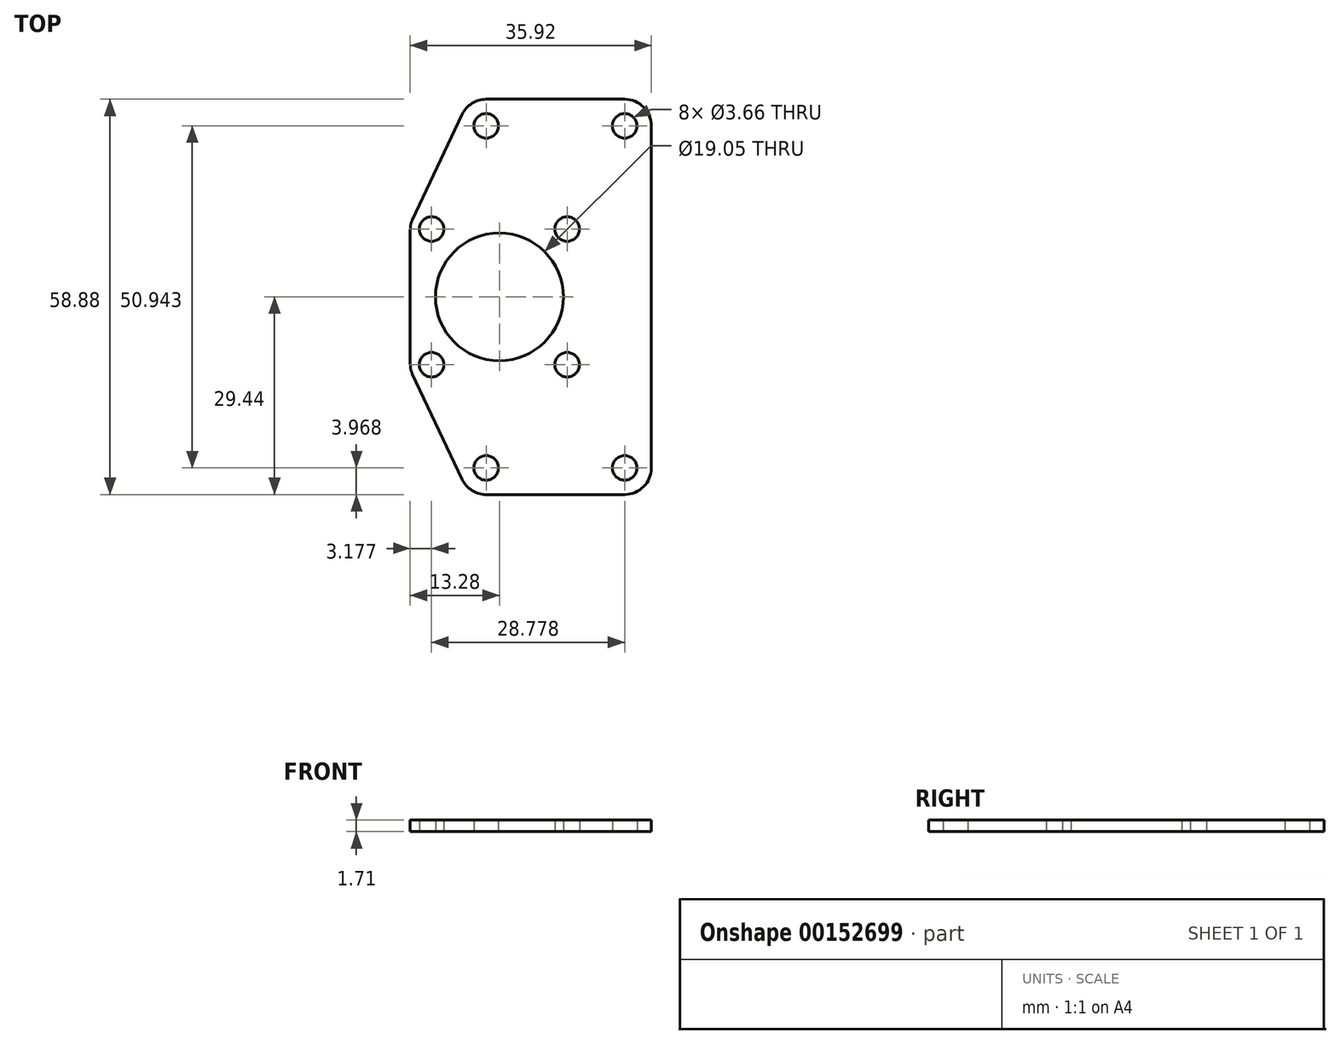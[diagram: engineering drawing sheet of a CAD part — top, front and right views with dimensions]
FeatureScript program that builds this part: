
annotation { "Feature Type Name" : "Feature", "Feature Type Description" : "" }
export const myFeature = defineFeature(function(context is Context, id is Id, definition is map)
    precondition{}
    {
        {
            var Q0;
            Q0=qCreatedBy(makeId("Top.planeOp"),FACE);
            var sketch = newSketch(context, id + "F0", { "sketchPlane" : qUnion([Q0])});
            skLineSegment(sketch, "E0.bottom", {"start": v(10.1, 10.1) * mm, "end": v(-10.1, 10.1) * mm, "construction": true});
            skLineSegment(sketch, "E0.top", {"start": v(10.1, -10.1) * mm, "end": v(-10.1, -10.1) * mm, "construction": true});
            skLineSegment(sketch, "E0.left", {"start": v(10.1, 10.1) * mm, "end": v(10.1, -10.1) * mm, "construction": true});
            skLineSegment(sketch, "E0.right", {"start": v(-10.1, 10.1) * mm, "end": v(-10.1, -10.1) * mm, "construction": true});
            skPoint(sketch, "E0.middle", {"position": v(0, 0) * mm});
            skCircle(sketch, "E1", {"center": v(0, 0) * mm, "radius": 9.53 * mm});
            skCircle(sketch, "E2", {"center": v(-10.1, 10.1) * mm, "radius": 1.83 * mm});
            skCircle(sketch, "E3", {"center": v(10.1, 10.1) * mm, "radius": 1.83 * mm});
            skCircle(sketch, "E4", {"center": v(10.1, -10.1) * mm, "radius": 1.83 * mm});
            skCircle(sketch, "E5", {"center": v(-10.1, -10.1) * mm, "radius": 1.83 * mm});
            skLineSegment(sketch, "E6", {"start": v(0, 0) * mm, "end": v(-13.28, 0) * mm, "construction": true});
            skLineSegment(sketch, "E7", {"start": v(0, 0) * mm, "end": v(22.64, 0) * mm, "construction": true});
            skLineSegment(sketch, "E8", {"start": v(-13.28, -10.1) * mm, "end": v(-13.28, 10.1) * mm});
            skLineSegment(sketch, "E9", {"start": v(-12.97, -11.46) * mm, "end": v(-5.55, -27.17) * mm});
            skLineSegment(sketch, "E10", {"start": v(-12.97, 11.46) * mm, "end": v(-5.55, 27.17) * mm});
            skLineSegment(sketch, "E11", {"start": v(22.64, -29.44) * mm, "end": v(22.64, 29.44) * mm});
            skLineSegment(sketch, "E12", {"start": v(22.64, 29.44) * mm, "end": v(-1.96, 29.44) * mm});
            skLineSegment(sketch, "E13", {"start": v(22.64, -29.44) * mm, "end": v(-1.96, -29.44) * mm});
            skArc(sketch, "E14", {"start": v(-1.96, 29.44) * mm, "mid": v(-4.09, 28.82) * mm, "end": v(-5.55, 27.17) * mm});
            skArc(sketch, "E15", {"start": v(-5.55, -27.17) * mm, "mid": v(-4.09, -28.82) * mm, "end": v(-1.96, -29.44) * mm});
            skCircle(sketch, "E16", {"center": v(-1.96, -25.47) * mm, "radius": 1.83 * mm});
            skCircle(sketch, "E17", {"center": v(-1.96, 25.47) * mm, "radius": 1.83 * mm});
            skLineSegment(sketch, "E18", {"start": v(18.67, -29.44) * mm, "end": v(18.67, -25.47) * mm, "construction": true});
            skLineSegment(sketch, "E19", {"start": v(18.67, -25.47) * mm, "end": v(22.64, -25.47) * mm, "construction": true});
            skLineSegment(sketch, "E20", {"start": v(18.67, 29.44) * mm, "end": v(18.67, 25.47) * mm, "construction": true});
            skCircle(sketch, "E21", {"center": v(18.67, -25.47) * mm, "radius": 1.83 * mm});
            skCircle(sketch, "E22", {"center": v(18.67, 25.47) * mm, "radius": 1.83 * mm});
            skCircle(sketch, "E23", {"center": v(0, 0) * mm, "radius": 11.11 * mm, "construction": true});
            skArc(sketch, "E24", {"start": v(-12.97, 11.46) * mm, "mid": v(-13.2, 10.8) * mm, "end": v(-13.28, 10.1) * mm});
            skArc(sketch, "E25", {"start": v(-13.28, -10.1) * mm, "mid": v(-13.2, -10.8) * mm, "end": v(-12.97, -11.46) * mm});
            skLineSegment(sketch, "E26", {"start": v(18.67, -25.47) * mm, "end": v(-1.96, -25.47) * mm, "construction": true});
            skLineSegment(sketch, "E27", {"start": v(18.67, 25.47) * mm, "end": v(-1.96, 25.47) * mm, "construction": true});
            skSolve(sketch);
        }
        {
            var Q0;
            Q0=qSketchRegion(id+"F0",true);
            extrude(context, id + "F1", {"entities" : qUnion([Q0]), "depth" : 1.7 * mm});
        }
        {
            var Q0;
            Q0=makeQuery(id+"F1.opExtrude","SWEPT_EDGE",EDGE,{"disambiguationData":[OSD([sQuery(id+"F0.wireOp",EDGE,"E11"),sQuery(id+"F0.wireOp",EDGE,"E13")])]});
            var Q1;
            Q1=makeQuery(id+"F1.opExtrude","SWEPT_EDGE",EDGE,{"disambiguationData":[OSD([sQuery(id+"F0.wireOp",EDGE,"E11"),sQuery(id+"F0.wireOp",EDGE,"E12")])]});
            fillet(context, id + "F2", {"entities" : qUnion([Q0, Q1]), "radius" : 3.97 * mm, "tangentPropagation" : true, "allowEdgeOverflow" : false});
        }
    });
